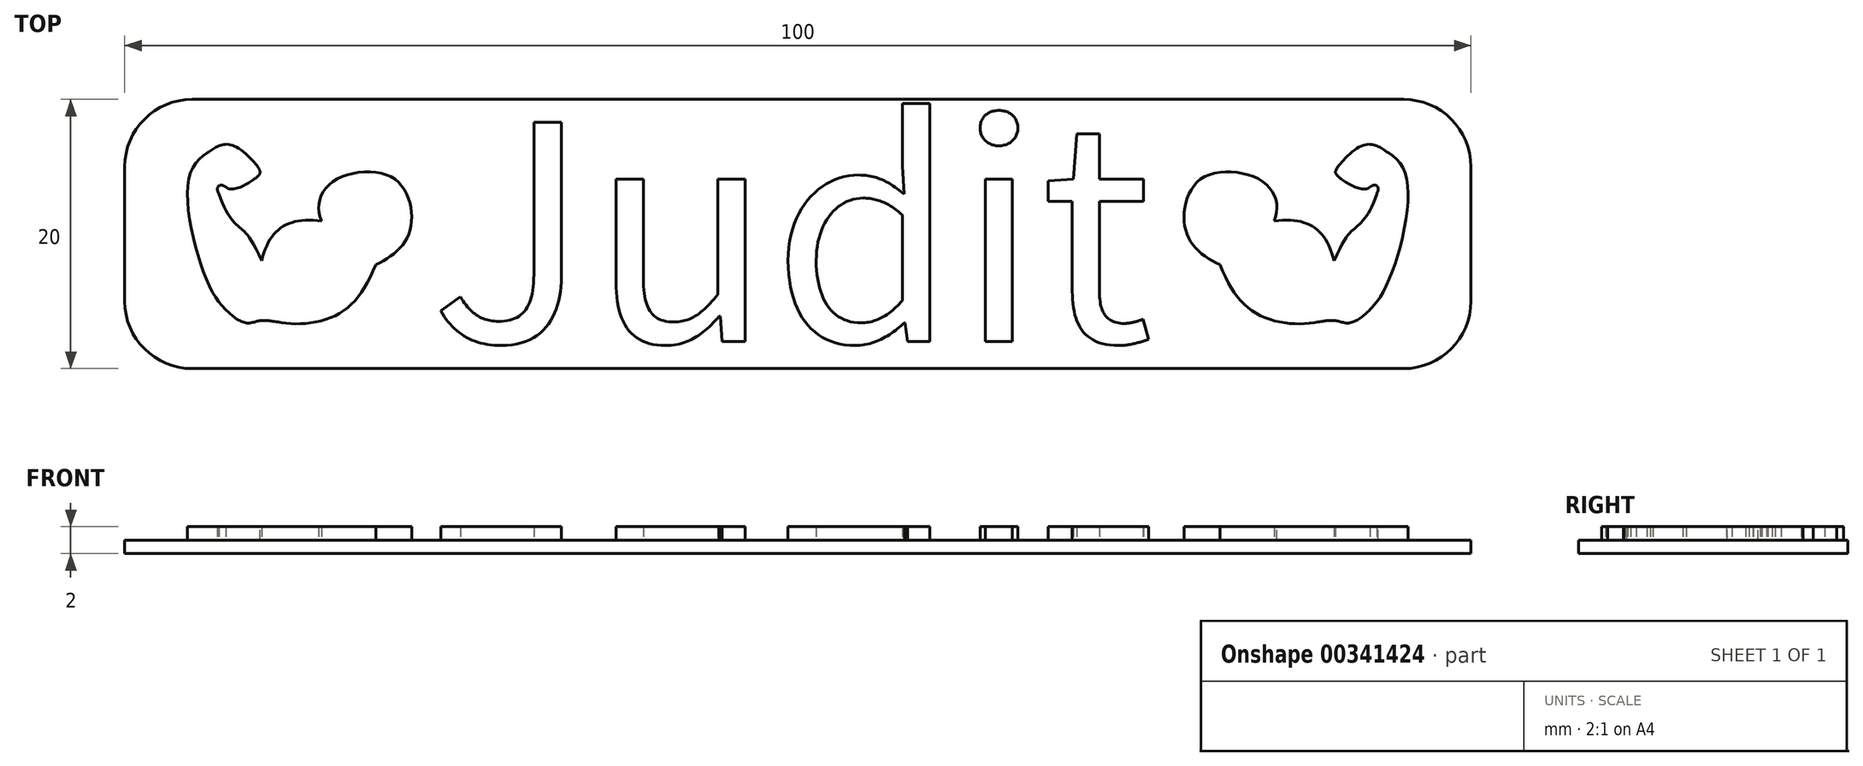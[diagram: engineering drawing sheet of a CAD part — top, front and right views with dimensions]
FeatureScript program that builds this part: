
annotation { "Feature Type Name" : "Feature", "Feature Type Description" : "" }
export const myFeature = defineFeature(function(context is Context, id is Id, definition is map)
    precondition{}
    {
        {
            var Q0;
            Q0=qCreatedBy(makeId("Top.planeOp"),FACE);
            var sketch = newSketch(context, id + "F0", { "sketchPlane" : qUnion([Q0])});
            skLineSegment(sketch, "E0.bottom", {"start": v(-50, 10) * mm, "end": v(50, 10) * mm});
            skLineSegment(sketch, "E0.top", {"start": v(-50, -10) * mm, "end": v(50, -10) * mm});
            skLineSegment(sketch, "E0.left", {"start": v(-50, 10) * mm, "end": v(-50, -10) * mm});
            skLineSegment(sketch, "E0.right", {"start": v(50, 10) * mm, "end": v(50, -10) * mm});
            skSolve(sketch);
        }
        {
            var Q0;
            Q0 = qSketchRegion(id + "F0", true);
            extrude(context, id + "F1", {"entities" : qUnion([Q0]), "depth" : 1 * mm});
        }
        {
            var Q0;
            Q0=makeQuery(id+"F1.opExtrude","CAP_FACE",FACE,{"disambiguationData":[OSD([sQuery(id+"F0.wireOp",EDGE,"E0.bottom"),sQuery(id+"F0.wireOp",EDGE,"E0.top"),sQuery(id+"F0.wireOp",EDGE,"E0.left"),sQuery(id+"F0.wireOp",EDGE,"E0.right")])],"isStart":false});
            var sketch = newSketch(context, id + "F2", { "sketchPlane" : qUnion([Q0])});
            skText(sketch, "E1", { "text": "Judit", "fontName": "NotoSansCJKjp-Regular.otf"});
            const initialGuessF2  = {"E1": [-0.0273, -0.008, 1, 0, 0.016]};
            skSetInitialGuess(sketch, initialGuessF2);
            skSolve(sketch);
        }
        {
            var Q0;
            Q0=makeQuery(id+"F2.imprint","IMPRINT",FACE,{"disambiguationData":[TD([[makeQuery(id+"F2.imprint","IMPRINT",EDGE,{"derivedFrom":sQuery(id+"F2.wireOp",EDGE,"E1.sketch_text.stroke-0")}),-1.0]])]});
            var sketch = newSketch(context, id + "F3", { "sketchPlane" : qUnion([Q0])});
            skFitSpline(sketch, "E2", {"points": [v(-37.66, 3.85) * mm, v(-42.46, 3.95) * mm, v(-43.38, 0.98) * mm], "startDerivative": vector(-5.34, 5.64) * mm, "endDerivative": vector(3.1, -7.09) * mm});
            skFitSpline(sketch, "E3", {"points": [v(-37.66, 3.85) * mm, v(-36.9, 0) * mm, v(-39.36, -2.27) * mm], "startDerivative": vector(5.69, -6) * mm, "endDerivative": vector(-6.7, -2.98) * mm});
            skFitSpline(sketch, "E4", {"points": [v(-46.34, -6.6) * mm, v(-42.4, -6.09) * mm, v(-39.36, -2.27) * mm], "startDerivative": vector(7.49, -1.22) * mm, "endDerivative": vector(4.48, 11.38) * mm});
            skFitSpline(sketch, "E5", {"points": [v(-46.34, -6.6) * mm, v(-48.5, -6.57) * mm], "startDerivative": vector(-3.55, 0.58) * mm, "endDerivative": vector(-2.41, -0.73) * mm});
            skFitSpline(sketch, "E6", {"points": [v(-48.5, -6.57) * mm, v(-50.77, -5.33) * mm], "startDerivative": vector(-2.41, -0.73) * mm, "endDerivative": vector(-1.87, 2) * mm});
            skFitSpline(sketch, "E7", {"points": [v(-50.77, -5.33) * mm, v(-52.5, -1.8) * mm, v(-53.23, 4.14) * mm, v(-51.86, 6.03) * mm], "startDerivative": vector(-5.63, 5.99) * mm, "endDerivative": vector(7.51, 4.7) * mm});
            skFitSpline(sketch, "E8", {"points": [v(-51.86, 6.03) * mm, v(-49, 5.94) * mm], "startDerivative": vector(1.93, 1.2) * mm, "endDerivative": vector(4.26, -4) * mm});
            skFitSpline(sketch, "E9", {"points": [v(-49, 5.94) * mm, v(-48.18, 4.24) * mm], "startDerivative": vector(4.26, -4) * mm, "endDerivative": vector(-0.82, -0.84) * mm});
            skFitSpline(sketch, "E10", {"points": [v(-48.18, 4.24) * mm, v(-50.5, 3.49) * mm], "startDerivative": vector(-0.82, -0.84) * mm, "endDerivative": vector(-1.73, 1.59) * mm});
            skFitSpline(sketch, "E11", {"points": [v(-51, 2.97) * mm, v(-49.57, 0.58) * mm, v(-47.83, -1.99) * mm], "startDerivative": vector(2.64, -8.49) * mm, "endDerivative": vector(5.19, -11.62) * mm});
            skFitSpline(sketch, "E12", {"points": [v(-47.83, -1.99) * mm, v(-43.38, 0.98) * mm], "startDerivative": vector(1.78, 7.29) * mm, "endDerivative": vector(7.52, -0.85) * mm});
            skFitSpline(sketch, "E13", {"points": [v(-51, 2.97) * mm, v(-51.12, 3.4) * mm, v(-50.92, 3.62) * mm, v(-50.63, 3.57) * mm, v(-50.5, 3.49) * mm], "startDerivative": vector(-0.69, 1.44) * mm, "endDerivative": vector(0.57, -0.45) * mm});
            skSolve(sketch);
        }
        {
            var Q0;
            Q0=makeQuery(id+"F2.imprint","IMPRINT",FACE,{"disambiguationData":[TD([[makeQuery(id+"F2.imprint","IMPRINT",EDGE,{"derivedFrom":sQuery(id+"F2.wireOp",EDGE,"E1.sketch_text.stroke-0")}),-1.0]])]});
            var sketch = newSketch(context, id + "F4", { "sketchPlane" : qUnion([Q0])});
            skLineSegment(sketch, "E14", {"start": v(50, 10) * mm, "end": v(30, -10) * mm, "construction": true});
            skLineSegment(sketch, "E15", {"start": v(40, 0) * mm, "end": v(30, 10) * mm, "construction": true});
            skLineSegment(sketch, "E16", {"start": v(33.28, 6.72) * mm, "end": v(33.99, 7.42) * mm});
            skLineSegment(sketch, "E17", {"start": v(33.99, 7.42) * mm, "end": v(34.7, 6.72) * mm});
            skLineSegment(sketch, "E18", {"start": v(34.7, 6.72) * mm, "end": v(36.46, 8.49) * mm});
            skLineSegment(sketch, "E19", {"start": v(36.46, 8.49) * mm, "end": v(38.23, 6.72) * mm});
            skLineSegment(sketch, "E20", {"start": v(38.23, 6.72) * mm, "end": v(36.46, 4.95) * mm});
            skLineSegment(sketch, "E21", {"start": v(36.46, 4.95) * mm, "end": v(36.82, 4.6) * mm});
            skLineSegment(sketch, "E22", {"start": v(36.82, 4.6) * mm, "end": v(40.35, 8.13) * mm});
            skLineSegment(sketch, "E23", {"start": v(40.35, 8.13) * mm, "end": v(42.12, 6.36) * mm});
            skLineSegment(sketch, "E24", {"start": v(42.12, 6.36) * mm, "end": v(38.59, 2.83) * mm});
            skLineSegment(sketch, "E25", {"start": v(38.59, 2.83) * mm, "end": v(40.7, 0.7) * mm});
            skLineSegment(sketch, "E26.MirrorCS", {"start": v(37.17, 1.41) * mm, "end": v(39.3, -0.7) * mm});
            skLineSegment(sketch, "E27.MirrorCS", {"start": v(33.64, -2.12) * mm, "end": v(37.17, 1.41) * mm});
            skLineSegment(sketch, "E28.MirrorCS", {"start": v(31.87, -0.35) * mm, "end": v(33.64, -2.12) * mm});
            skLineSegment(sketch, "E29.MirrorCS", {"start": v(35.4, 3.18) * mm, "end": v(31.87, -0.35) * mm});
            skLineSegment(sketch, "E30.MirrorCS", {"start": v(33.28, 1.77) * mm, "end": v(35.05, 3.54) * mm});
            skLineSegment(sketch, "E31.MirrorCS", {"start": v(35.05, 3.54) * mm, "end": v(35.4, 3.18) * mm});
            skLineSegment(sketch, "E32.MirrorCS", {"start": v(31.51, 3.54) * mm, "end": v(33.28, 1.77) * mm});
            skLineSegment(sketch, "E33.MirrorCS", {"start": v(33.28, 5.3) * mm, "end": v(31.51, 3.54) * mm});
            skLineSegment(sketch, "E34.MirrorCS", {"start": v(32.58, 6.01) * mm, "end": v(33.28, 5.3) * mm});
            skLineSegment(sketch, "E35.MirrorCS", {"start": v(33.28, 6.72) * mm, "end": v(32.58, 6.01) * mm});
            skLineSegment(sketch, "E36.MirrorCS", {"start": v(42.83, -1.41) * mm, "end": v(40.7, 0.7) * mm});
            skLineSegment(sketch, "E37.MirrorCS", {"start": v(41.41, -2.83) * mm, "end": v(39.3, -0.7) * mm});
            skLineSegment(sketch, "E38.MirrorCS", {"start": v(46.36, 2.12) * mm, "end": v(42.83, -1.41) * mm});
            skLineSegment(sketch, "E39.MirrorCS", {"start": v(37.88, -6.36) * mm, "end": v(41.41, -2.83) * mm});
            skLineSegment(sketch, "E40.MirrorCS", {"start": v(39.65, -8.13) * mm, "end": v(37.88, -6.36) * mm});
            skLineSegment(sketch, "E41.MirrorCS", {"start": v(48.13, 0.35) * mm, "end": v(46.36, 2.12) * mm});
            skLineSegment(sketch, "E42.MirrorCS", {"start": v(44.6, -3.18) * mm, "end": v(48.13, 0.35) * mm});
            skLineSegment(sketch, "E43.MirrorCS", {"start": v(43.18, -4.6) * mm, "end": v(39.65, -8.13) * mm});
            skLineSegment(sketch, "E44.MirrorCS", {"start": v(43.54, -4.95) * mm, "end": v(43.18, -4.6) * mm});
            skLineSegment(sketch, "E45.MirrorCS", {"start": v(44.95, -3.54) * mm, "end": v(44.6, -3.18) * mm});
            skLineSegment(sketch, "E46.MirrorCS", {"start": v(46.72, -1.77) * mm, "end": v(44.95, -3.54) * mm});
            skLineSegment(sketch, "E47.MirrorCS", {"start": v(41.77, -6.72) * mm, "end": v(43.54, -4.95) * mm});
            skLineSegment(sketch, "E48.MirrorCS", {"start": v(43.54, -8.49) * mm, "end": v(41.77, -6.72) * mm});
            skLineSegment(sketch, "E49.MirrorCS", {"start": v(48.49, -3.54) * mm, "end": v(46.72, -1.77) * mm});
            skLineSegment(sketch, "E50.MirrorCS", {"start": v(46.72, -5.3) * mm, "end": v(48.49, -3.54) * mm});
            skLineSegment(sketch, "E51.MirrorCS", {"start": v(45.3, -6.72) * mm, "end": v(43.54, -8.49) * mm});
            skLineSegment(sketch, "E52.MirrorCS", {"start": v(46.01, -7.42) * mm, "end": v(45.3, -6.72) * mm});
            skLineSegment(sketch, "E53.MirrorCS", {"start": v(47.42, -6.01) * mm, "end": v(46.72, -5.3) * mm});
            skLineSegment(sketch, "E54.MirrorCS", {"start": v(46.72, -6.72) * mm, "end": v(47.42, -6.01) * mm});
            skLineSegment(sketch, "E55.MirrorCS", {"start": v(46.72, -6.72) * mm, "end": v(46.01, -7.42) * mm});
            skSolve(sketch);
        }
        {
            var Q0;
            Q0=makeQuery(id+"F1.opExtrude","SWEPT_EDGE",EDGE,{"disambiguationData":[OSD([sQuery(id+"F0.wireOp",EDGE,"E0.bottom"),sQuery(id+"F0.wireOp",EDGE,"E0.left")])]});
            var Q1;
            Q1=makeQuery(id+"F1.opExtrude","SWEPT_EDGE",EDGE,{"disambiguationData":[OSD([sQuery(id+"F0.wireOp",EDGE,"E0.top"),sQuery(id+"F0.wireOp",EDGE,"E0.left")])]});
            var Q2;
            Q2=makeQuery(id+"F1.opExtrude","SWEPT_EDGE",EDGE,{"disambiguationData":[OSD([sQuery(id+"F0.wireOp",EDGE,"E0.top"),sQuery(id+"F0.wireOp",EDGE,"E0.right")])]});
            var Q3;
            Q3=makeQuery(id+"F1.opExtrude","SWEPT_EDGE",EDGE,{"disambiguationData":[OSD([sQuery(id+"F0.wireOp",EDGE,"E0.bottom"),sQuery(id+"F0.wireOp",EDGE,"E0.right")])]});
            fillet(context, id + "F5", {"entities" : qUnion([Q0, Q1, Q2, Q3]), "radius" : 5 * mm, "tangentPropagation" : true, "allowEdgeOverflow" : false});
        }
        {
            var Q0;
            Q0 = qSketchRegion(id + "F2", true);
            extrude(context, id + "F6", {"entities" : qUnion([Q0]), "operationType" : NewBodyOperationType.ADD, "depth" : 1 * mm});
        }
        {
            var Q0;
            Q0 = qSketchRegion(id + "F3", true);
            extrude(context, id + "F7", {"entities" : qUnion([Q0]), "depth" : 1 * mm});
        }
        {
            var Q0;
            Q0=makeQuery(id+"F7.opExtrude","SWEPT_BODY",BODY,{"disambiguationData":[OSD([sQuery(id+"F3.wireOp",EDGE,"E2"),sQuery(id+"F3.wireOp",EDGE,"E3"),sQuery(id+"F3.wireOp",EDGE,"E4"),sQuery(id+"F3.wireOp",EDGE,"E5"),sQuery(id+"F3.wireOp",EDGE,"E6"),sQuery(id+"F3.wireOp",EDGE,"E7"),sQuery(id+"F3.wireOp",EDGE,"E8"),sQuery(id+"F3.wireOp",EDGE,"E9"),sQuery(id+"F3.wireOp",EDGE,"E10"),sQuery(id+"F3.wireOp",EDGE,"E11"),sQuery(id+"F3.wireOp",EDGE,"E12"),sQuery(id+"F3.wireOp",EDGE,"E13")])]});
            transform(context, id + "F8", {"entities" : qUnion([Q0]), "transformType" : TransformType.TRANSLATION_3D, "dx" : 8 * mm, "dy" : 0 * mm, "dz" : 0 * mm, "makeCopy" : false});
        }
        {
            var Q0;
            Q0=makeQuery(id+"F7.opExtrude","SWEPT_BODY",BODY,{"disambiguationData":[OSD([sQuery(id+"F3.wireOp",EDGE,"E2"),sQuery(id+"F3.wireOp",EDGE,"E3"),sQuery(id+"F3.wireOp",EDGE,"E4"),sQuery(id+"F3.wireOp",EDGE,"E5"),sQuery(id+"F3.wireOp",EDGE,"E6"),sQuery(id+"F3.wireOp",EDGE,"E7"),sQuery(id+"F3.wireOp",EDGE,"E8"),sQuery(id+"F3.wireOp",EDGE,"E9"),sQuery(id+"F3.wireOp",EDGE,"E10"),sQuery(id+"F3.wireOp",EDGE,"E11"),sQuery(id+"F3.wireOp",EDGE,"E12"),sQuery(id+"F3.wireOp",EDGE,"E13")])]});
            var Q1;
            Q1=qCreatedBy(makeId("Right.planeOp"),FACE);
            mirror(context, id + "F9", {"operationType" : NewBodyOperationType.ADD, "entities" : qUnion([Q0]), "mirrorPlane" : qUnion([Q1])});
        }
    });
